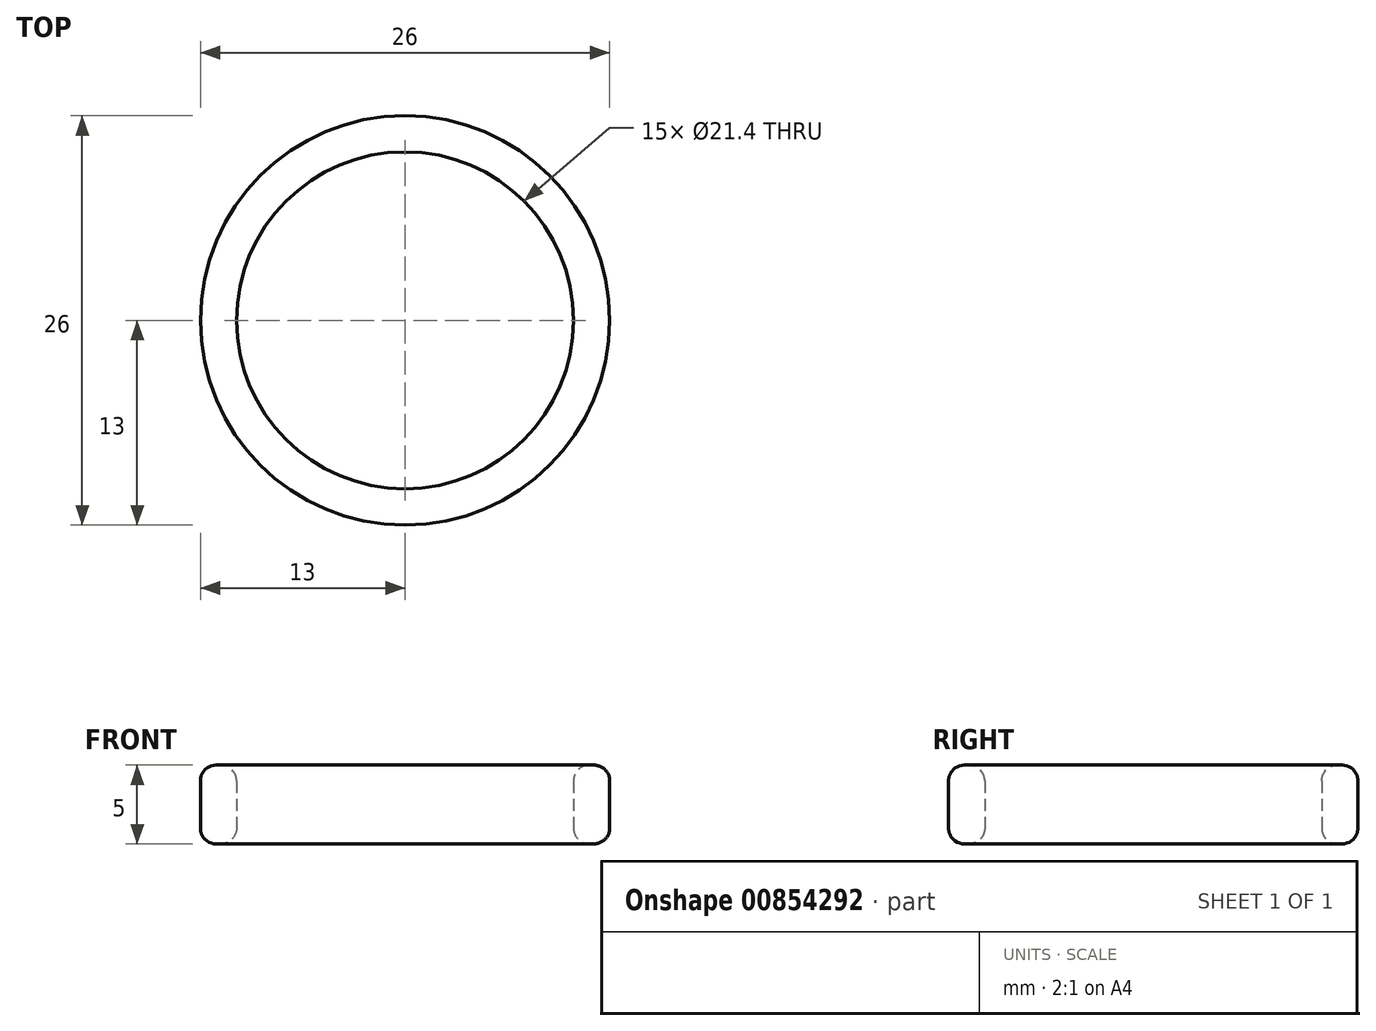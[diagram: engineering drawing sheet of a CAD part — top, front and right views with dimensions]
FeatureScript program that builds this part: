
annotation { "Feature Type Name" : "Feature", "Feature Type Description" : "" }
export const myFeature = defineFeature(function(context is Context, id is Id, definition is map)
    precondition{}
    {
        {
            var Q0;
            Q0=qCreatedBy(makeId("Top.planeOp"),FACE);
            var sketch = newSketch(context, id + "F0", { "sketchPlane" : qUnion([Q0])});
            skCircle(sketch, "E0", {"center": v(0, 0) * mm, "radius": 10.7 * mm});
            skCircle(sketch, "E1", {"center": v(0, 0) * mm, "radius": 13 * mm});
            skSolve(sketch);
        }
        {
            var Q0;
            Q0=makeQuery(id+"F0.imprint","IMPRINT",FACE,{"disambiguationData":[TD([[makeQuery(id+"F0.imprint","IMPRINT",EDGE,{"derivedFrom":sQuery(id+"F0.wireOp",EDGE,"E0")}),-1.0]])]});
            extrude(context, id + "F1", {"entities" : qUnion([Q0]), "depth" : 5 * mm, "offsetDistance" : 25 * mm});
        }
        {
            var Q0;
            Q0=makeQuery(id+"F1.opExtrude","CAP_EDGE",EDGE,{"disambiguationData":[OSD([sQuery(id+"F0.wireOp",EDGE,"E1")])],"isStart":false});
            var Q1;
            Q1=makeQuery(id+"F1.opExtrude","CAP_EDGE",EDGE,{"disambiguationData":[OSD([sQuery(id+"F0.wireOp",EDGE,"E1")])],"isStart":true});
            var Q2;
            Q2=makeQuery(id+"F1.opExtrude","CAP_EDGE",EDGE,{"disambiguationData":[OSD([sQuery(id+"F0.wireOp",EDGE,"E0")])],"isStart":true});
            var Q3;
            Q3=makeQuery(id+"F1.opExtrude","CAP_EDGE",EDGE,{"disambiguationData":[OSD([sQuery(id+"F0.wireOp",EDGE,"E0")])],"isStart":false});
            fillet(context, id + "F2", {"entities" : qUnion([Q0, Q1, Q2, Q3]), "radius" : 1 * mm, "tangentPropagation" : true, "allowEdgeOverflow" : false});
        }
    });
